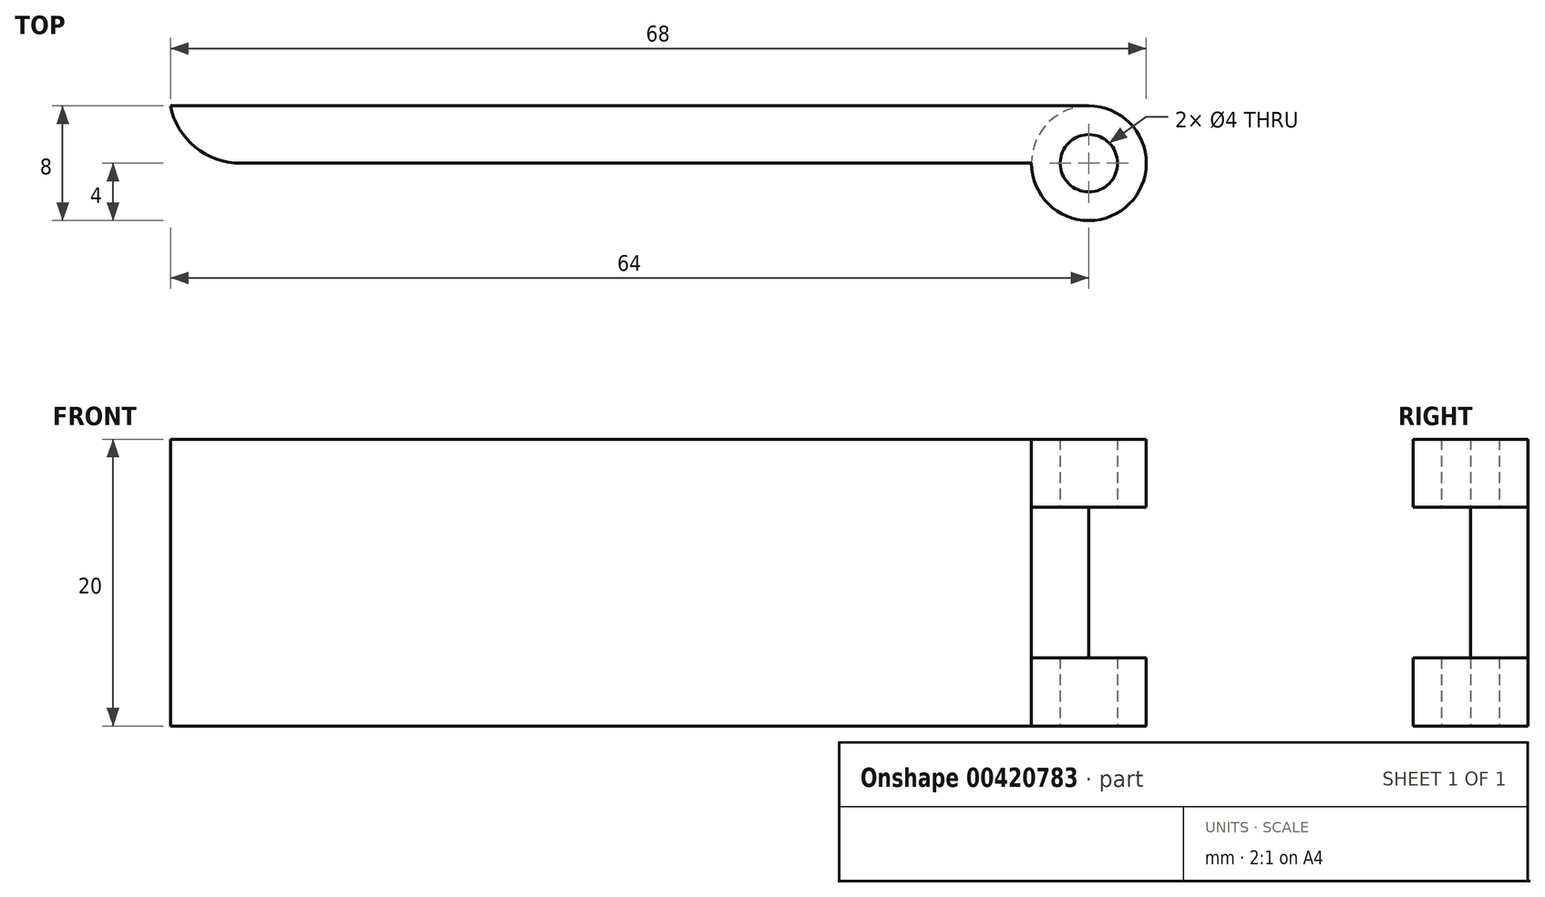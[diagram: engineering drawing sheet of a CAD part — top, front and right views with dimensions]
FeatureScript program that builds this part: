
annotation { "Feature Type Name" : "Feature", "Feature Type Description" : "" }
export const myFeature = defineFeature(function(context is Context, id is Id, definition is map)
    precondition{}
    {
        {
            var Q0;
            Q0=qCreatedBy(makeId("Top.planeOp"),FACE);
            var sketch = newSketch(context, id + "F0", { "sketchPlane" : qUnion([Q0])});
            skLineSegment(sketch, "E0.bottom", {"start": v(0, 0) * mm, "end": v(64, 0) * mm});
            skLineSegment(sketch, "E0.top", {"start": v(0, -4) * mm, "end": v(60, -4) * mm});
            skLineSegment(sketch, "E0.left", {"start": v(0, 0) * mm, "end": v(0, -4) * mm});
            skCircle(sketch, "E1", {"center": v(64, -4) * mm, "radius": 4 * mm});
            skCircle(sketch, "E2", {"center": v(64, -4) * mm, "radius": 2 * mm});
            skSolve(sketch);
        }
        {
            var Q0;
            {var subQ0=sQuery(id+"F0.wireOp",EDGE,"E0.bottom");Q0=makeQuery(id+"F0.imprint","IMPRINT",FACE,{"disambiguationData":[TD([[makeQuery(id+"F0.imprint","IMPRINT",EDGE,{"derivedFrom":subQ0}),-1.0]])]});}
            var Q1;
            Q1=makeQuery(id+"F0.imprint","IMPRINT",FACE,{"disambiguationData":[TD([[makeQuery(id+"F0.imprint","IMPRINT",EDGE,{"derivedFrom":sQuery(id+"F0.wireOp",EDGE,"E2")}),-1.0]])]});
            extrude(context, id + "F1", {"entities" : qUnion([Q0, Q1]), "endBound" : BoundingType.SYMMETRIC, "depth" : 20 * mm});
        }
        {
            var Q0;
            Q0=makeQuery(id+"F0.imprint","IMPRINT",FACE,{"disambiguationData":[TD([[makeQuery(id+"F0.imprint","IMPRINT",EDGE,{"derivedFrom":sQuery(id+"F0.wireOp",EDGE,"E2")}),-1.0]])]});
            extrude(context, id + "F2", {"entities" : qUnion([Q0]), "operationType" : NewBodyOperationType.REMOVE, "endBound" : BoundingType.SYMMETRIC, "oppositeDirection" : true, "depth" : 10.5 * mm});
        }
        {
            var Q0;
            Q0=makeQuery(id+"F1.opExtrude","SWEPT_EDGE",EDGE,{"disambiguationData":[OSD([sQuery(id+"F0.wireOp",EDGE,"E0.top"),sQuery(id+"F0.wireOp",EDGE,"E0.left")])]});
            fillet(context, id + "F3", {"entities" : qUnion([Q0]), "radius" : 5 * mm, "tangentPropagation" : true, "allowEdgeOverflow" : false});
        }
    });
